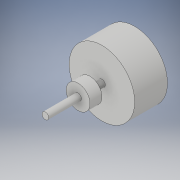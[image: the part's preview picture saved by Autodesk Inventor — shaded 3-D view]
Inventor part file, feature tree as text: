
AUTODESK INVENTOR PART (.ipt)
format: ipt  version: 2018.2 (Build 222227000, 227)  size: 112,128 bytes
history: native  units: in
note: dims shown in document units (in); Inventor stores cm internally (conversion verified against a paired STEP export)
features: extrude x4, sketch x4
ambient origin geometry x8: Origin, YZ Plane, XZ Plane, XY Plane, X Axis, Y Axis, Z Axis, Center Point
bodies: Solid1 (feature_tree)
feature tree (8):
  extrude  "Extrusion1"  Depth=0.8661in TaperAngle=0.0deg
  extrude  "Extrusion2"  Depth=0.315in TaperAngle=0.0deg
  extrude  "Extrusion3"  Depth=0.315in TaperAngle=0.0deg
  extrude  "Extrusion4"  [1 undecoded]
  sketch  "Sketch1"  dims[d0=1.7323in d1=0.8661in d2=0.0in]
  sketch  "Sketch2"  dims[d3=0.1772in d4=0.315in d5=0.0in]
  sketch  "Sketch3"  dims[d6=0.6299in d7=0.315in d8=0.0in]
  sketch  "Sketch4"  dims[d9=0.8661in d10=0.0in]
note: 1 required parameter value undecoded (feature->parameter linkage not recoverable at this tier; creation-order binding heuristic only, values carry confidence <= 0.55)
